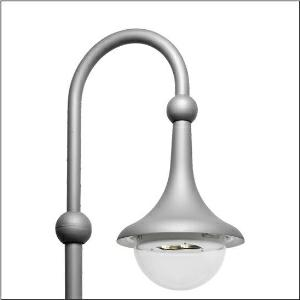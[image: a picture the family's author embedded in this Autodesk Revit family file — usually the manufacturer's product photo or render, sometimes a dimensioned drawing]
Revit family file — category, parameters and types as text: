
# Revit family: grosse_glocke_iq___st1_2a_5xa1565k1f108_5d30
name_source: partatom
category: Lighting Fixtures
units: mm (PartAtom-declared; Revit-internal decimal feet)

## family parameters
Cut with Voids When Loaded = No
Host = Face
Light Source = No
Part Type = Normal
Room Calculation Point = No
Round Connector Dimension = Use Diameter
Shared = No

## types (1)
- --- (1 x LED, 5420 lm, 34.3 W, 4000K)
    Apparent Load = 34 VA
    CIE Flux Codes = 28 66 95 100 100
    Color Rendering = 70
    Color Temperature = 4000K
    Default Elevation = 1800 mm
    Description = Large Bell iQ, mast luminaire, primary light control with 3 zone facetted reflector, of plastic, silver coated, primary optical cover: enclosure, of PMMA, transparent, light distribution: ST1.2a, light emission: direct distribution, primary light characteristic: asymmetric, installation type: suspended mounting, High Power LED, rated luminous flux: 5.420lm, luminous efficacy: 158lm/W, light colour: 740, colour temperature: 4000K, control gear: iQ Street-Remote, control: optimised constant luminous flux control (CLO 2.0), Desk-Remote (wireless, voltage-free reading and setting of iQ features in the workshop via application-optimized NFC function/RFID function), Light-Fading, Smart-Wire, Night-Set, Lumen-Switch, Temp-Guard, Auto-Match, Street-Remote, pre-setting: logarithmic dimming characteristic, mains connection: 230..240V, AC, 50/60Hz, start of lifetime: 34W, end of service life: 38W, reduction: 16W, luminaire housing, bell-shaped, of glass-fibre reinforced polyester, coated, Siteco® metallic grey (DB 702S), please order curved mast extension separately, diameter: 530mm, height: 695mm, mounting height: 4..6m, protection rating (complete): IP54, insulation class (complete): insulation class II (safety insulation), certification: CE, ENEC, VDE, impact resistance: IK08, standard-compliant lighting for roads and squares, packaging unit: 1 piece

Light Distribution: ST1.2a
    Height = 695 mm
    Lamp = 1 x LED
    Lamp Light Flux = 5420 lm
    Lamp Power = 34.3 W
    Lamp count = 1
    Length = 530 mm
    Luminous efficacy = 158 lm/W
    Manufacturer = Siteco
    ModVariant = No
    Model = 5XA1565K1F108
    Mounting Place = Pole
    Mounting Type = Pole annexe
    Number of Poles = 1
    OnlyDefault = Yes
    Power Factor = 1
    Product Name = Große Glocke iQ | ST1.2a
    Product group = mast luminaire | pylon annexe
    ProductGroupID = 6200
    Protection Class = Protection class II
    Protection Degree = IP 54
    RLX_Detail_Level = 1
    RLX_Emergency_Light_Flux = 0 lm
    RLX_Emergency_Type = 0
    RLX_Emergency_Type_DB = No
    RlxData = <blob elided: 85365 chars, md5=6c7c055a>
    Socket = socket
    Standby Power = 0 W
    System Light Flux = 5420 lm
    System Power = 34 W
    Type Comments = factory setting: luminous flux: 100 % | dim-lin: 254 | 640 mA
    Type Image = l_1347688.jpg
    URL = http://relux.com
    VarID = @adj_067761
    Voltage = 0 V
    Weight = 0.00 kg
    Width = 0 mm  [stored 0 ft]

note: [stored X ft] marks values corroborated as IEEE doubles in the binary element streams (Revit-internal decimal feet)

## geometry (parser evidence)
native form markers: Blend x4, Sweep x13
no freeform markers — native parametric forms only
